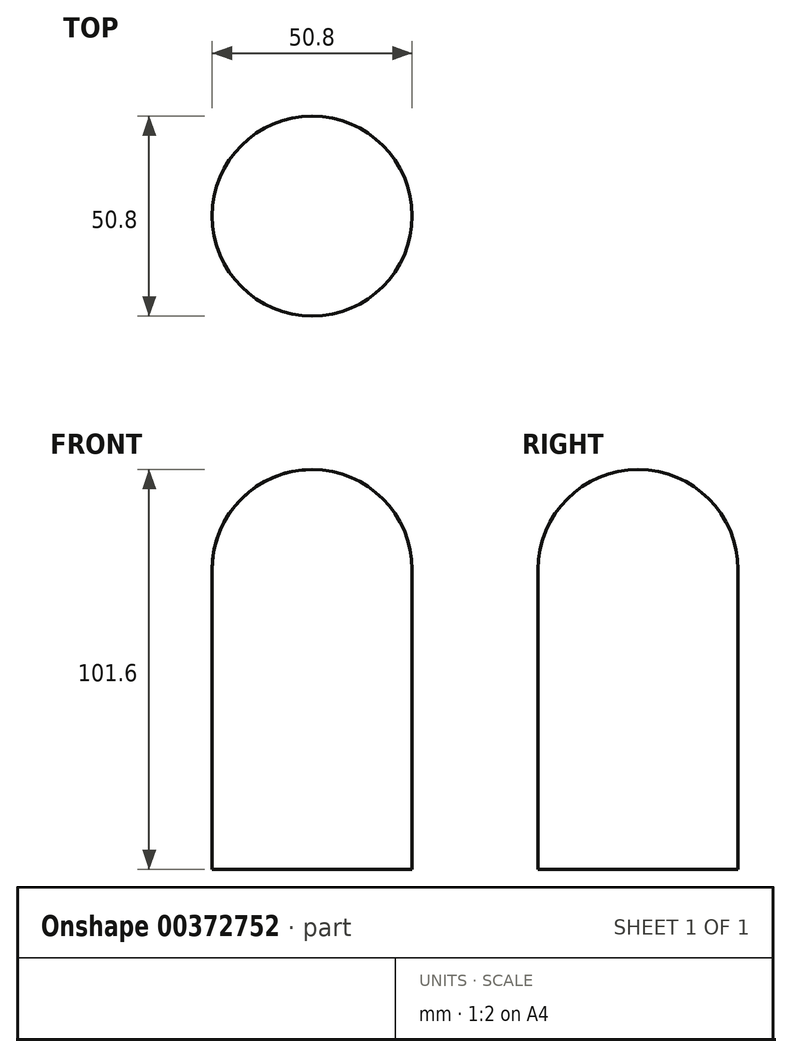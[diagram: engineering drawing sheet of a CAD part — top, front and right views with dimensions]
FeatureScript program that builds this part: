
annotation { "Feature Type Name" : "Feature", "Feature Type Description" : "" }
export const myFeature = defineFeature(function(context is Context, id is Id, definition is map)
    precondition{}
    {
        {
            var Q0;
            Q0=qCreatedBy(makeId("Front.planeOp"),FACE);
            var sketch = newSketch(context, id + "F0", { "sketchPlane" : qUnion([Q0])});
            skLineSegment(sketch, "E0", {"start": v(0, -38.1) * mm, "end": v(-25.4, -38.1) * mm});
            skLineSegment(sketch, "E1", {"start": v(-25.4, -38.1) * mm, "end": v(-25.4, 38.1) * mm});
            skArc(sketch, "E2", {"start": v(0, 63.5) * mm, "mid": v(-17.96, 56.06) * mm, "end": v(-25.4, 38.1) * mm});
            skLineSegment(sketch, "E3", {"start": v(0, -38.1) * mm, "end": v(0, 63.5) * mm});
            skSolve(sketch);
        }
        {
            var Q0;
            Q0=makeQuery(id+"F0.imprint","IMPRINT",FACE,{"disambiguationData":[TD([[makeQuery(id+"F0.imprint","IMPRINT",EDGE,{"derivedFrom":sQuery(id+"F0.wireOp",EDGE,"E0")}),-1.0]])]});
            var Q1;
            Q1=sQuery(id+"F0.wireOp",EDGE,"E3");
            revolve(context, id + "F1", {"entities" : qUnion([Q0]), "axis" : qUnion([Q1]), "revolveType" : RevolveType.FULL});
        }
    });
